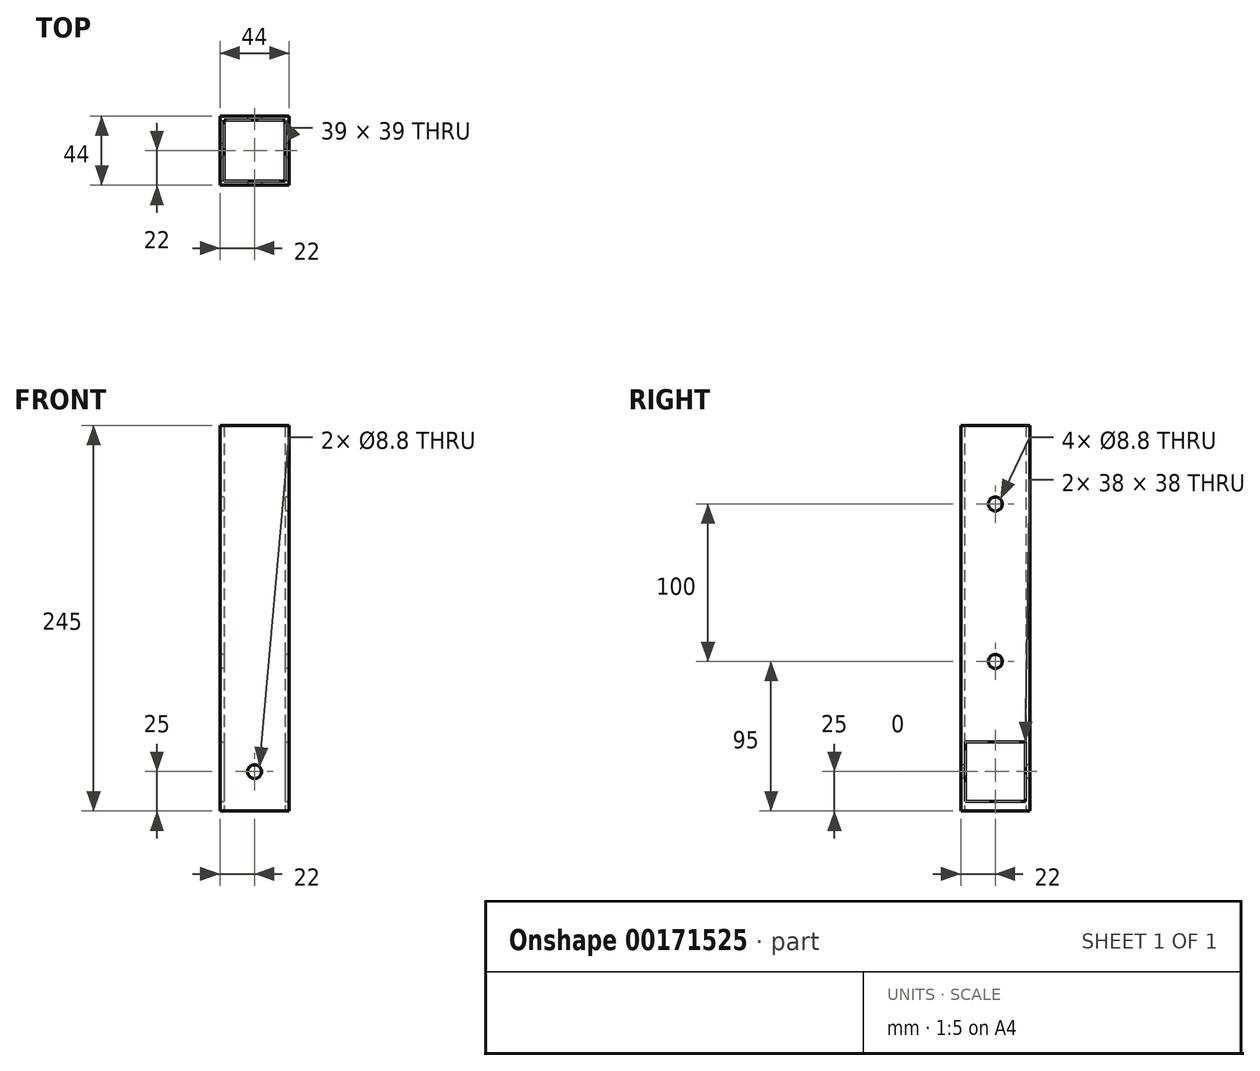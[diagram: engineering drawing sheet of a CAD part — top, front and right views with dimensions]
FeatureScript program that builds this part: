
annotation { "Feature Type Name" : "Feature", "Feature Type Description" : "" }
export const myFeature = defineFeature(function(context is Context, id is Id, definition is map)
    precondition{}
    {
        {
            var Q0;
            Q0=qCreatedBy(makeId("Top.planeOp"),FACE);
            var sketch = newSketch(context, id + "F0", { "sketchPlane" : qUnion([Q0])});
            skLineSegment(sketch, "E0.bottom", {"start": v(22, -22) * mm, "end": v(-22, -22) * mm});
            skLineSegment(sketch, "E0.top", {"start": v(22, 22) * mm, "end": v(-22, 22) * mm});
            skLineSegment(sketch, "E0.left", {"start": v(22, -22) * mm, "end": v(22, 22) * mm});
            skLineSegment(sketch, "E0.right", {"start": v(-22, -22) * mm, "end": v(-22, 22) * mm});
            skPoint(sketch, "E0.middle", {"position": v(0, 0) * mm});
            skLineSegment(sketch, "E1.bottom", {"start": v(19.5, -19.5) * mm, "end": v(-19.5, -19.5) * mm});
            skLineSegment(sketch, "E1.top", {"start": v(19.5, 19.5) * mm, "end": v(-19.5, 19.5) * mm});
            skLineSegment(sketch, "E1.left", {"start": v(19.5, -19.5) * mm, "end": v(19.5, 19.5) * mm});
            skLineSegment(sketch, "E1.right", {"start": v(-19.5, -19.5) * mm, "end": v(-19.5, 19.5) * mm});
            skSolve(sketch);
        }
        {
            var Q0;
            Q0=makeQuery(id+"F0.imprint","IMPRINT",FACE,{"disambiguationData":[TD([[makeQuery(id+"F0.imprint","IMPRINT",EDGE,{"derivedFrom":sQuery(id+"F0.wireOp",EDGE,"E0.bottom")}),-1.0]])]});
            extrude(context, id + "F1", {"entities" : qUnion([Q0]), "depth" : 245 * mm});
        }
        {
            var Q0;
            Q0=makeQuery(id+"F1.opExtrude","SWEPT_FACE",FACE,{"disambiguationData":[OSD([sQuery(id+"F0.wireOp",EDGE,"E0.right")])]});
            var sketch = newSketch(context, id + "F2", { "sketchPlane" : qUnion([Q0])});
            skPoint(sketch, "E2", {"position": v(0, 195) * mm});
            skPoint(sketch, "E2.positionSnap0", {"position": v(0, 245) * mm});
            skPoint(sketch, "E3", {"position": v(0, 95) * mm});
            skSolve(sketch);
        }
        {
            var Q0;
            Q0=sQuery(id+"F2.wireOp",VERTEX,"E2");
            var Q1;
            Q1=sQuery(id+"F2.wireOp",VERTEX,"E3");
            var Q2;
            Q2=makeQuery(id+"F1.opExtrude","SWEPT_BODY",BODY,{"disambiguationData":[OSD([sQuery(id+"F0.wireOp",EDGE,"E0.bottom"),sQuery(id+"F0.wireOp",EDGE,"E0.top"),sQuery(id+"F0.wireOp",EDGE,"E0.left"),sQuery(id+"F0.wireOp",EDGE,"E0.right"),sQuery(id+"F0.wireOp",EDGE,"E1.bottom"),sQuery(id+"F0.wireOp",EDGE,"E1.top"),sQuery(id+"F0.wireOp",EDGE,"E1.left"),sQuery(id+"F0.wireOp",EDGE,"E1.right")])]});
            hole(context, id + "F3", {"style" : HoleStyle.SIMPLE, "endStyle" : HoleEndStyle.THROUGH, "standardTappedOrClearance" : lookupTablePath({ "standard" : "ISO", "fit" : "Normal", "size" : "M8", "type" : "Clearance" }), "standardBlindInLast" : lookupTablePath({ "fit" : "Standard", "standard" : "ISO", "size" : "M8", "type" : "Clearance" }), "holeDiameter" : 8.8 * mm, "locations" : qUnion([Q0, Q1]), "scope" : qUnion([Q2]), "isTappedThrough" : true});
        }
        {
            var Q0;
            Q0=makeQuery(id+"F1.opExtrude","SWEPT_FACE",FACE,{"disambiguationData":[OSD([sQuery(id+"F0.wireOp",EDGE,"E0.left")])]});
            var sketch = newSketch(context, id + "F4", { "sketchPlane" : qUnion([Q0])});
            skLineSegment(sketch, "E4.bottom", {"start": v(19, 6) * mm, "end": v(-19, 6) * mm});
            skLineSegment(sketch, "E4.top", {"start": v(19, 44) * mm, "end": v(-19, 44) * mm});
            skLineSegment(sketch, "E4.left", {"start": v(19, 6) * mm, "end": v(19, 44) * mm});
            skLineSegment(sketch, "E4.right", {"start": v(-19, 6) * mm, "end": v(-19, 44) * mm});
            skPoint(sketch, "E4.middle.positionSnap0", {"position": v(0, 0) * mm});
            skPoint(sketch, "E4.centerSnap0", {"position": v(0, 0) * mm});
            skSolve(sketch);
        }
        {
            var Q0;
            Q0=makeQuery(id+"F4.imprint","IMPRINT",FACE,{"disambiguationData":[TD([[makeQuery(id+"F4.imprint","IMPRINT",EDGE,{"derivedFrom":sQuery(id+"F4.wireOp",EDGE,"E4.bottom")}),-1.0]])]});
            extrude(context, id + "F5", {"entities" : qUnion([Q0]), "operationType" : NewBodyOperationType.REMOVE, "endBound" : BoundingType.THROUGH_ALL, "oppositeDirection" : true, "depth" : 25 * mm});
        }
        {
            var Q0;
            Q0=makeQuery(id+"F1.opExtrude","SWEPT_FACE",FACE,{"disambiguationData":[OSD([sQuery(id+"F0.wireOp",EDGE,"E0.bottom")])]});
            var sketch = newSketch(context, id + "F6", { "sketchPlane" : qUnion([Q0])});
            skPoint(sketch, "E5", {"position": v(0, 25) * mm});
            skPoint(sketch, "E5.positionSnap0", {"position": v(0, 0) * mm});
            skSolve(sketch);
        }
        {
            var Q0;
            Q0=sQuery(id+"F6.wireOp",VERTEX,"E5");
            var Q1;
            Q1=makeQuery(id+"F1.opExtrude","SWEPT_BODY",BODY,{"disambiguationData":[OSD([sQuery(id+"F0.wireOp",EDGE,"E0.bottom"),sQuery(id+"F0.wireOp",EDGE,"E0.top"),sQuery(id+"F0.wireOp",EDGE,"E0.left"),sQuery(id+"F0.wireOp",EDGE,"E0.right"),sQuery(id+"F0.wireOp",EDGE,"E1.bottom"),sQuery(id+"F0.wireOp",EDGE,"E1.top"),sQuery(id+"F0.wireOp",EDGE,"E1.left"),sQuery(id+"F0.wireOp",EDGE,"E1.right")])]});
            hole(context, id + "F7", {"style" : HoleStyle.SIMPLE, "endStyle" : HoleEndStyle.THROUGH, "standardTappedOrClearance" : lookupTablePath({ "standard" : "ISO", "fit" : "Normal", "size" : "M8", "type" : "Clearance" }), "standardBlindInLast" : lookupTablePath({ "fit" : "Standard", "standard" : "ISO", "size" : "M8", "type" : "Clearance" }), "holeDiameter" : 8.8 * mm, "locations" : qUnion([Q0]), "scope" : qUnion([Q1]), "isTappedThrough" : true});
        }
    });
